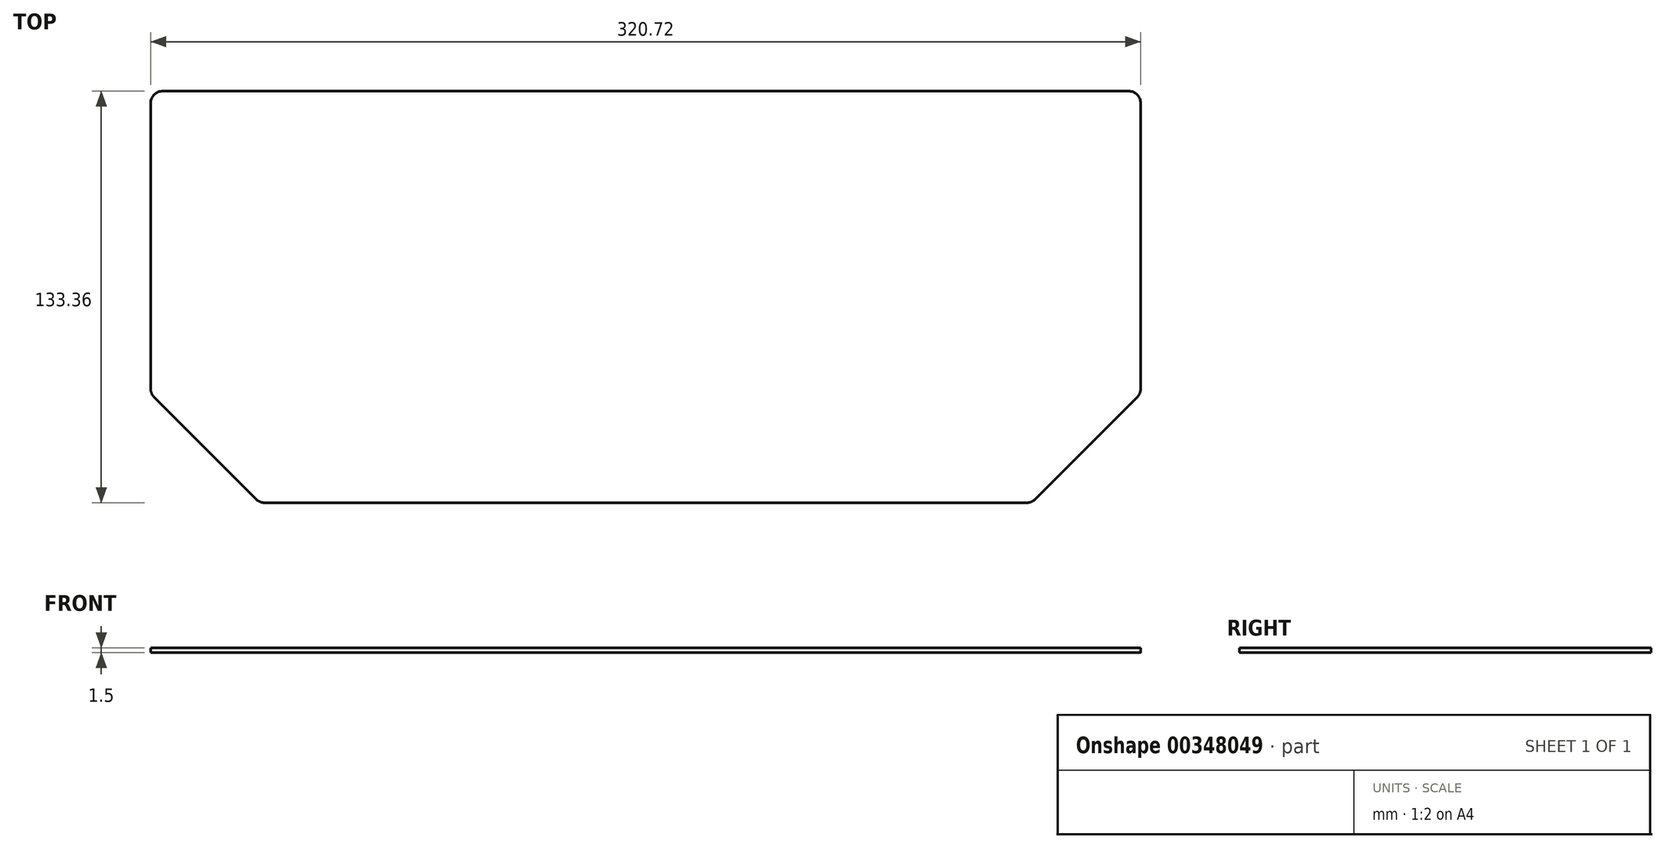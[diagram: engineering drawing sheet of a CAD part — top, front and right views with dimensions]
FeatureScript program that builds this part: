
annotation { "Feature Type Name" : "Feature", "Feature Type Description" : "" }
export const myFeature = defineFeature(function(context is Context, id is Id, definition is map)
    precondition{}
    {
        {
            var Q0;
            Q0=qCreatedBy(makeId("Top.planeOp"),FACE);
            var sketch = newSketch(context, id + "F0", { "sketchPlane" : qUnion([Q0])});
            skLineSegment(sketch, "E0", {"start": v(-125, -50) * mm, "end": v(125, -50) * mm});
            skPoint(sketch, "E1", {"position": v(0, -50) * mm});
            skLineSegment(sketch, "E2", {"start": v(-160.36, -14.64) * mm, "end": v(-125, -50) * mm});
            skLineSegment(sketch, "E3", {"start": v(125, -50) * mm, "end": v(160.36, -14.64) * mm});
            skLineSegment(sketch, "E4", {"start": v(-160.36, -14.64) * mm, "end": v(-160.36, 83.36) * mm});
            skLineSegment(sketch, "E5", {"start": v(160.36, -14.64) * mm, "end": v(160.36, 83.36) * mm});
            skLineSegment(sketch, "E6", {"start": v(-160.36, 83.36) * mm, "end": v(160.36, 83.36) * mm});
            skLineSegment(sketch, "E7.0", {"start": v(-145.36, -8.43) * mm, "end": v(-118.79, -35) * mm});
            skLineSegment(sketch, "E7.1", {"start": v(-145.36, 68.36) * mm, "end": v(145.36, 68.36) * mm});
            skLineSegment(sketch, "E7.2", {"start": v(145.36, -8.43) * mm, "end": v(145.36, 68.36) * mm});
            skLineSegment(sketch, "E7.3", {"start": v(-145.36, -8.43) * mm, "end": v(-145.36, 68.36) * mm});
            skLineSegment(sketch, "E7.4", {"start": v(118.79, -35) * mm, "end": v(145.36, -8.43) * mm});
            skLineSegment(sketch, "E7.5", {"start": v(-118.79, -35) * mm, "end": v(118.79, -35) * mm});
            skSolve(sketch);
        }
        {
            var Q0;
            Q0=makeQuery(id+"F0.imprint","IMPRINT",FACE,{"disambiguationData":[TD([[makeQuery(id+"F0.imprint","IMPRINT",EDGE,{"derivedFrom":sQuery(id+"F0.wireOp",EDGE,"Vh9EBWVG-A7LR-WKkb-vcs5-wTAlFZ58apW8.bottom")}),-1.0]])]});
            var Q1;
            Q1=makeQuery(id+"F0.imprint","IMPRINT",FACE,{"disambiguationData":[TD([[makeQuery(id+"F0.imprint","IMPRINT",EDGE,{"derivedFrom":sQuery(id+"F0.wireOp",EDGE,"E7.0")}),1.0]])]});
            var Q2;
            Q2=makeQuery(id+"F0.imprint","IMPRINT",FACE,{"disambiguationData":[TD([[makeQuery(id+"F0.imprint","IMPRINT",EDGE,{"derivedFrom":sQuery(id+"F0.wireOp",EDGE,"E0")}),1.0]])]});
            extrude(context, id + "F1", {"entities" : qUnion([Q0, Q1, Q2]), "depth" : 1.5 * mm});
        }
        {
            var Q0;
            Q0=makeQuery(id+"F1.opExtrude","SWEPT_EDGE",EDGE,{"disambiguationData":[OSD([sQuery(id+"F0.wireOp",EDGE,"E3"),sQuery(id+"F0.wireOp",EDGE,"E5")])]});
            var Q1;
            Q1=makeQuery(id+"F1.opExtrude","SWEPT_EDGE",EDGE,{"disambiguationData":[OSD([sQuery(id+"F0.wireOp",EDGE,"E0"),sQuery(id+"F0.wireOp",EDGE,"E3")])]});
            var Q2;
            Q2=makeQuery(id+"F1.opExtrude","SWEPT_EDGE",EDGE,{"disambiguationData":[OSD([sQuery(id+"F0.wireOp",EDGE,"E5"),sQuery(id+"F0.wireOp",EDGE,"E6")])]});
            var Q3;
            Q3=makeQuery(id+"F1.opExtrude","SWEPT_EDGE",EDGE,{"disambiguationData":[OSD([sQuery(id+"F0.wireOp",EDGE,"E0"),sQuery(id+"F0.wireOp",EDGE,"E2")])]});
            var Q4;
            Q4=makeQuery(id+"F1.opExtrude","SWEPT_EDGE",EDGE,{"disambiguationData":[OSD([sQuery(id+"F0.wireOp",EDGE,"E2"),sQuery(id+"F0.wireOp",EDGE,"E4")])]});
            var Q5;
            Q5=makeQuery(id+"F1.opExtrude","SWEPT_EDGE",EDGE,{"disambiguationData":[OSD([sQuery(id+"F0.wireOp",EDGE,"E4"),sQuery(id+"F0.wireOp",EDGE,"E6")])]});
            fillet(context, id + "F2", {"entities" : qUnion([Q0, Q1, Q2, Q3, Q4, Q5]), "radius" : 4 * mm, "tangentPropagation" : true, "allowEdgeOverflow" : false});
        }
    });
